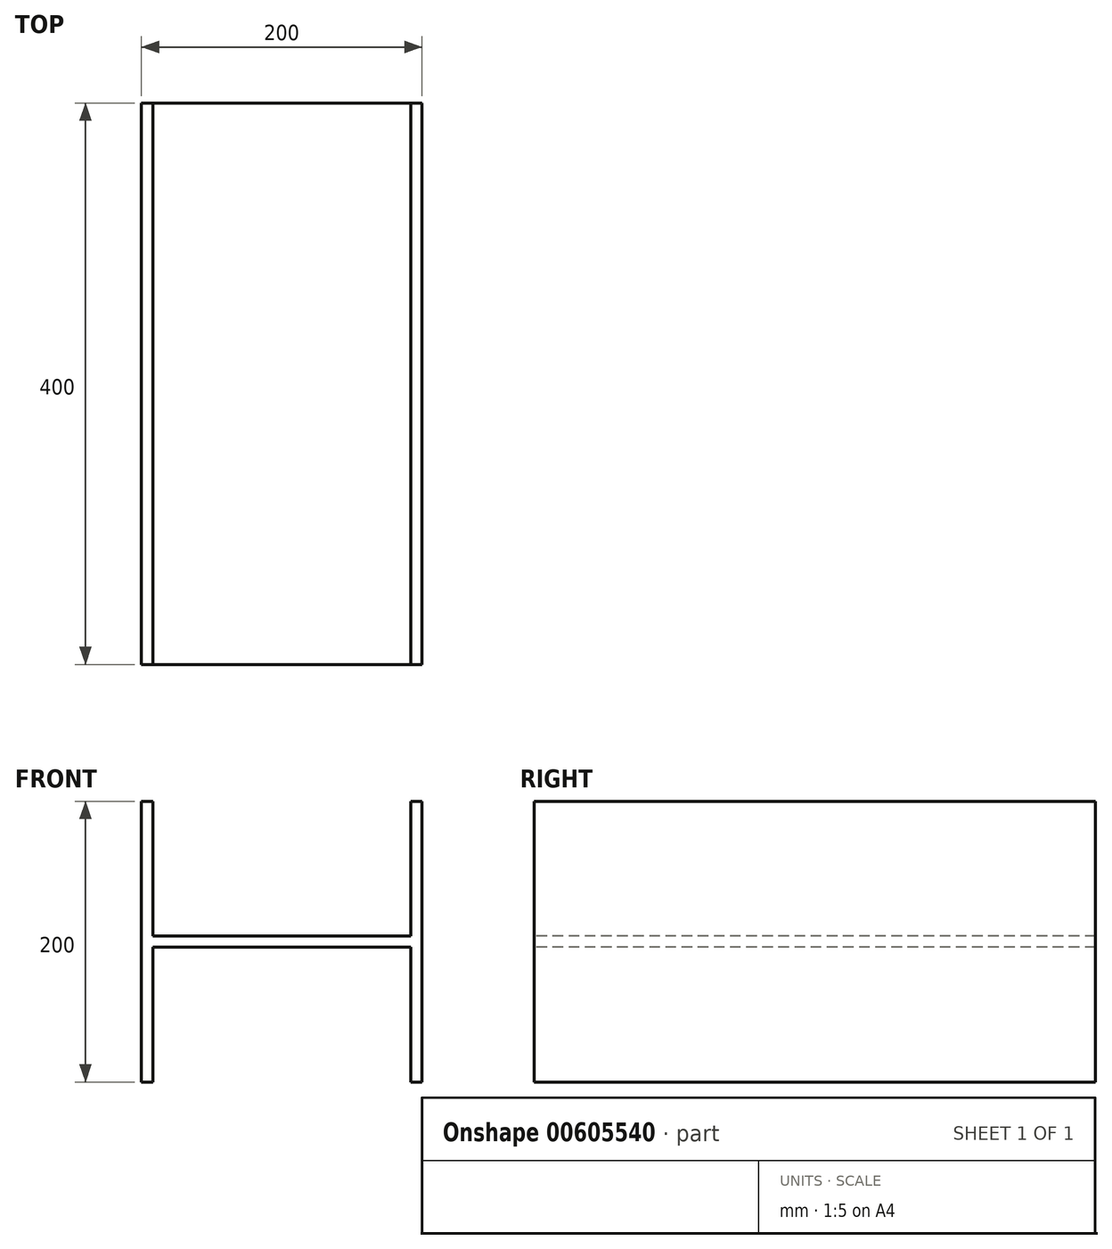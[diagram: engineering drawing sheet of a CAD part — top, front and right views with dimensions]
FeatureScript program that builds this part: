
annotation { "Feature Type Name" : "Feature", "Feature Type Description" : "" }
export const myFeature = defineFeature(function(context is Context, id is Id, definition is map)
    precondition{}
    {
        {
            var Q0;
            Q0=qCreatedBy(makeId("Front.planeOp"),FACE);
            var sketch = newSketch(context, id + "F0", { "sketchPlane" : qUnion([Q0])});
            skLineSegment(sketch, "E0.bottom", {"start": v(0, 0) * mm, "end": v(8, 0) * mm});
            skLineSegment(sketch, "E0.top", {"start": v(0, 200) * mm, "end": v(8, 200) * mm});
            skLineSegment(sketch, "E0.left", {"start": v(0, 0) * mm, "end": v(0, 200) * mm});
            skLineSegment(sketch, "E0.right", {"start": v(8, 0) * mm, "end": v(8, 200) * mm});
            skLineSegment(sketch, "E1.bottom", {"start": v(8, 104) * mm, "end": v(192, 104) * mm});
            skLineSegment(sketch, "E1.top", {"start": v(8, 96) * mm, "end": v(192, 96) * mm});
            skLineSegment(sketch, "E1.left", {"start": v(8, 104) * mm, "end": v(8, 96) * mm});
            skLineSegment(sketch, "E1.right", {"start": v(192, 104) * mm, "end": v(192, 96) * mm});
            skPoint(sketch, "E1.middle", {"position": v(100, 100) * mm});
            skPoint(sketch, "E1.middle.positionSnap0", {"position": v(8, 100) * mm});
            skPoint(sketch, "E1.centerSnap0", {"position": v(8, 100) * mm});
            skLineSegment(sketch, "E2.bottom", {"start": v(192, 0) * mm, "end": v(200, 0) * mm});
            skLineSegment(sketch, "E2.top", {"start": v(192, 200) * mm, "end": v(200, 200) * mm});
            skLineSegment(sketch, "E2.left", {"start": v(192, 0) * mm, "end": v(192, 200) * mm});
            skLineSegment(sketch, "E2.right", {"start": v(200, 0) * mm, "end": v(200, 200) * mm});
            skSolve(sketch);
        }
        {
            var Q0;
            Q0 = qSketchRegion(id + "F0", true);
            extrude(context, id + "F1", {"entities" : qUnion([Q0]), "oppositeDirection" : true, "depth" : 400 * mm, "offsetDistance" : 25 * mm});
        }
    });
